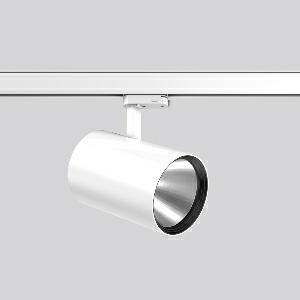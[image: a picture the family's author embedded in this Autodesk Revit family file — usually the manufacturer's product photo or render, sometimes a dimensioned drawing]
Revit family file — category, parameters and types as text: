
# Revit family: deecos_s_maxi_742234_002_c45b
name_source: partatom
category: Lighting Fixtures
units: mm (PartAtom-declared; Revit-internal decimal feet)

## family parameters
Cut with Voids When Loaded = No
Host = Face
Light Source = No
Part Type = Normal
Room Calculation Point = No
Round Connector Dimension = Use Diameter
Shared = No

## types (1)
- DEECOS S maxi (1 x LED Modul 920 meat+, 2200 lm, 2000)
    Apparent Load = 33 VA
    Approval mark = CE
    CIE Flux Codes = 100 100 100 100 100
    Color Rendering = 90
    Color Temperature = 2000
    Default Elevation = 1800 mm
    Description = Series: DEECOS S maxi
LED surface-mounted projector in modern design with no visible cooling ribs. Housing: die-cast aluminium, powder-coated. Rotation range: 356°. Swivel range: 90°. Black plastic ring and recessed LED to prevent glare from the side. Optical assembly with reflector made of MIRO-Silver with 98% total light reflection for outstanding efficiency - can be changed without tools. Special LED for illumination of meat included. With multi adaptor for 3-circuit tracks 230 V. Suitable for Track on ceiling, Wall track. High quality converter without flickering and stroboscopic effect. The following accessories can be mounted without use of tools: interchangeable lenses, decorative glasses, honeycomb louvre, clear and frosted diffusers, white interchangeable plastic ring. 
Colour: traffic white, matt (RAL 9016)
Diameter: 123 mm
Height: 200 mm
Lamp: LED
Socket: without socket
Colour temperature: meat +
System power: 33 W
Rated luminous flux: 2200 lm
Luminous efficiency: 67 lm/W
Control gear: Regulated power supply
Protection class: I
Type of protection: IP 20
    Height = 200 mm  [stored 0.656168 ft]
    Lamp = 1 x LED Modul 920 meat+
    Lamp Light Flux = 2200 lm
    Lamp count = 1
    Length = 123 mm
    Lifetime = 50000 h
    Luminous efficacy = 67 lm/W
    Manufacturer = RZB
    ModVariant = No
    Model = 742234.002
    Mounting Place = Ceiling
    Mounting Type = Rail mounted
    Number of Poles = 1
    OnlyDefault = Yes
    Power Factor = 1
    Product Name = DEECOS S maxi
    Product group = Track mounted projectors
    ProductGroupID = 301
    Protection Class = Protection class I
    Protection Degree = IP 20
    RLX_Detail_Level = 1
    RLX_Emergency_Light_Flux = 0 lm
    RLX_Emergency_Type = 0
    RLX_Emergency_Type_DB = No
    RlxData = <blob elided: 38517 chars, md5=152e32e0>
    Socket = socket
    Standby Power = 0 W
    System Light Flux = 2200 lm
    System Power = 33 W
    Type Comments = Product without accessories
    Type Image = 741954.002.jpg
    URL = http://relux.com
    VarID = ---
    Voltage = 230 V
    Voltage Range = 220-240 V
    Weight = 0.00 kg
    Width = 0 mm  [stored 0 ft]

note: [stored X ft] marks values corroborated as IEEE doubles in the binary element streams (Revit-internal decimal feet)

## geometry (parser evidence)
native form markers: Blend x4, Sweep x10
no freeform markers — native parametric forms only
